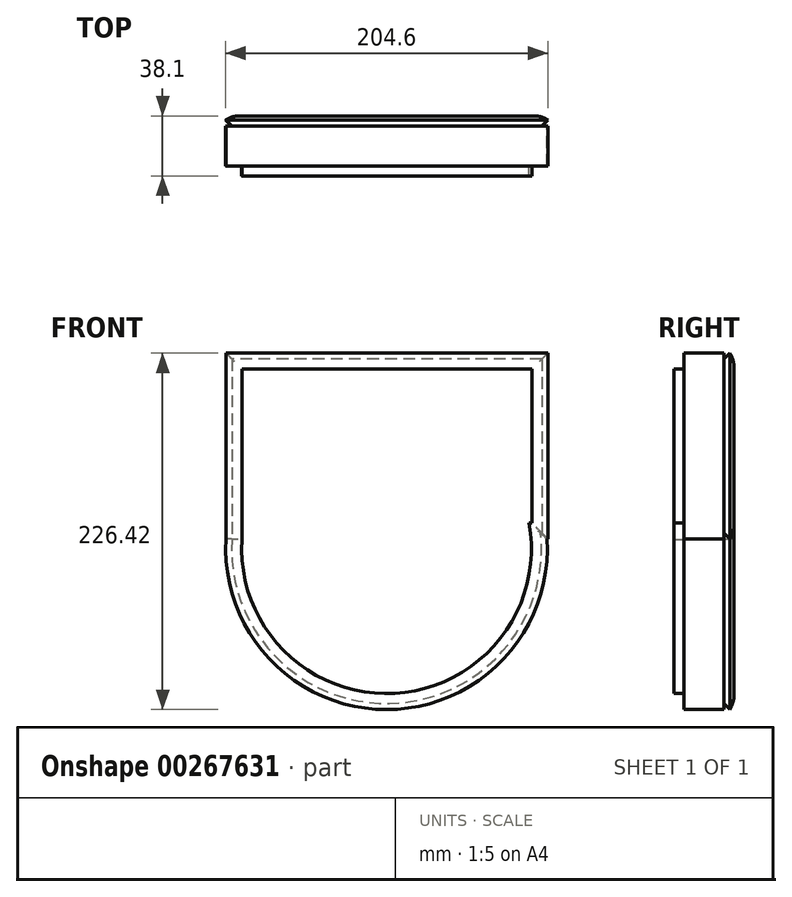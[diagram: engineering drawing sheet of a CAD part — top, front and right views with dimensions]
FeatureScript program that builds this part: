
annotation { "Feature Type Name" : "Feature", "Feature Type Description" : "" }
export const myFeature = defineFeature(function(context is Context, id is Id, definition is map)
    precondition{}
    {
        {
            var Q0;
            Q0=qCreatedBy(makeId("Front.planeOp"),FACE);
            var sketch = newSketch(context, id + "F0", { "sketchPlane" : qUnion([Q0])});
            skCircle(sketch, "E0", {"center": v(0, 0) * mm, "radius": 102.16 * mm});
            skLineSegment(sketch, "E1.bottom", {"start": v(-101.97, 6.14) * mm, "end": v(102.44, 6.14) * mm});
            skLineSegment(sketch, "E1.top", {"start": v(-101.97, 124.26) * mm, "end": v(102.44, 124.26) * mm});
            skLineSegment(sketch, "E1.left", {"start": v(-101.97, 6.14) * mm, "end": v(-101.97, 124.26) * mm});
            skLineSegment(sketch, "E1.right", {"start": v(102.44, 6.14) * mm, "end": v(102.44, 124.26) * mm});
            skSolve(sketch);
        }
        {
            var Q0;
            Q0 = qSketchRegion(id + "F0", true);
            extrude(context, id + "F1", {"entities" : qUnion([Q0]), "endBound" : BoundingType.SYMMETRIC, "depth" : 12.7 * mm});
        }
        {
            var Q0;
            Q0=makeQuery(id+"F1.opExtrude","CAP_FACE",FACE,{"disambiguationData":[OSD([sQuery(id+"F0.wireOp",EDGE,"E0")])],"isStart":false});
            chamfer(context, id + "F2", {"entities" : qUnion([Q0]), "width" : 10.16 * mm, "tangentPropagation" : true});
        }
        {
            var Q0;
            Q0=makeQuery(id+"F1.opExtrude","CAP_FACE",FACE,{"disambiguationData":[OSD([sQuery(id+"F0.wireOp",EDGE,"E0")])],"isStart":true});
            fillet(context, id + "F3", {"entities" : qUnion([Q0]), "radius" : 12.7 * mm, "tangentPropagation" : true, "rho" : 0.4, "crossSection" : FilletCrossSection.CONIC, "allowEdgeOverflow" : false});
        }
        {
            var Q0;
            Q0 = qSketchRegion(id + "F0", true);
            var Q1;
            Q1=makeQuery(id+"F1.opExtrude","CAP_FACE",FACE,{"disambiguationData":[OSD([sQuery(id+"F0.wireOp",EDGE,"E0"),sQuery(id+"F0.wireOp",EDGE,"E1.bottom"),sQuery(id+"F0.wireOp",EDGE,"E1.top"),sQuery(id+"F0.wireOp",EDGE,"E1.left"),sQuery(id+"F0.wireOp",EDGE,"E1.right")])],"isStart":false});
            extrude(context, id + "F4", {"entities" : qUnion([Q0, Q1]), "operationType" : NewBodyOperationType.ADD, "depth" : 25.4 * mm});
        }
    });
